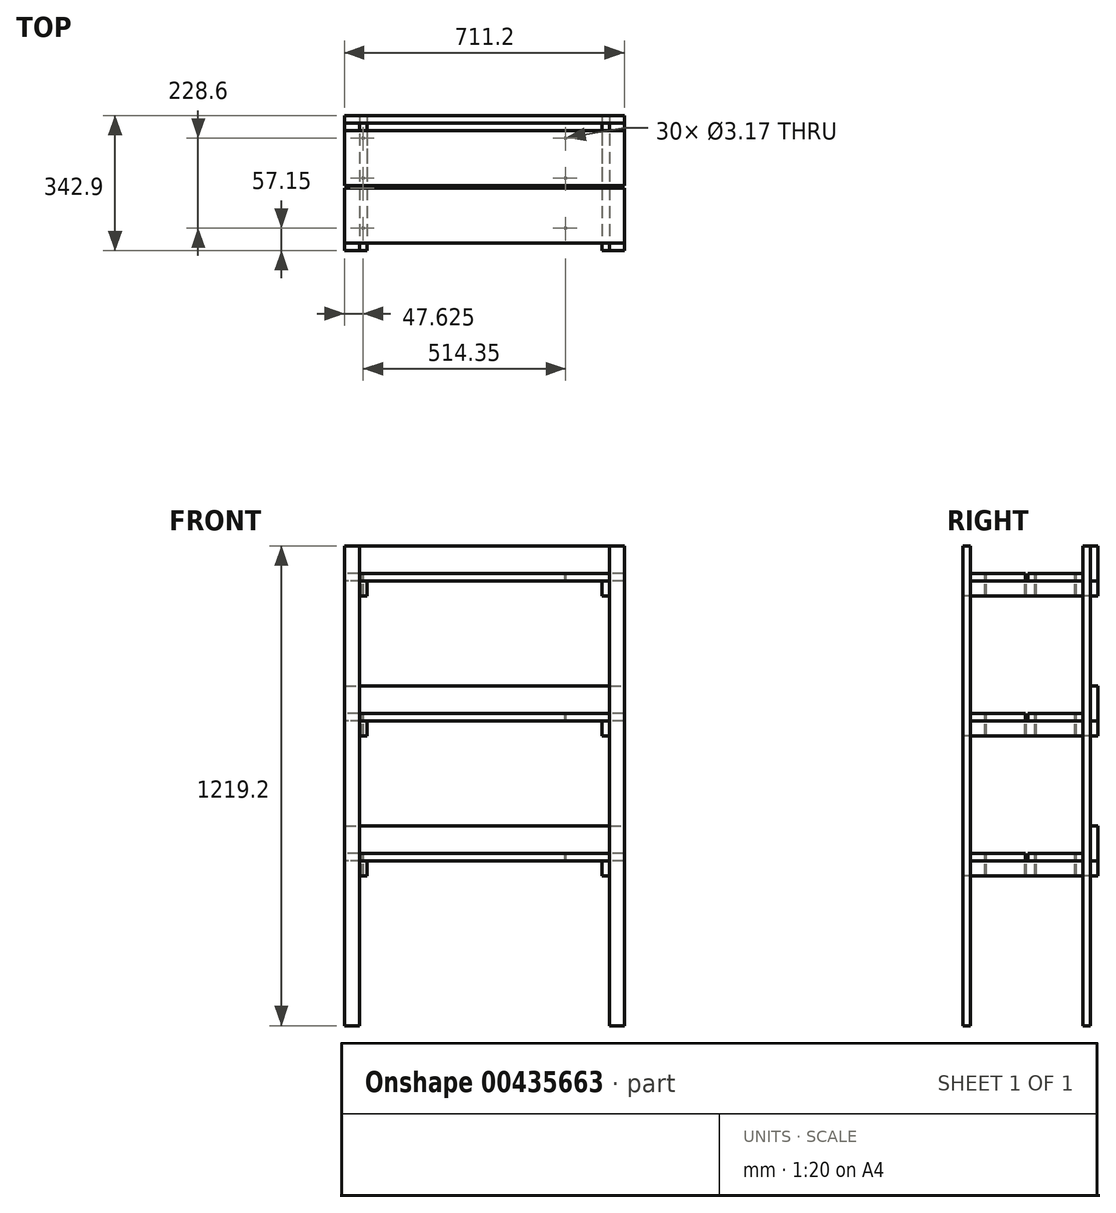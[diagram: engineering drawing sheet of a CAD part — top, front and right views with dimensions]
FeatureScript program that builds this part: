
annotation { "Feature Type Name" : "Feature", "Feature Type Description" : "" }
export const myFeature = defineFeature(function(context is Context, id is Id, definition is map)
    precondition{}
    {
        {
            var Q0;
            Q0=qCreatedBy(makeId("Top.planeOp"),FACE);
            var sketch = newSketch(context, id + "F0", { "sketchPlane" : qUnion([Q0])});
            skLineSegment(sketch, "E0.bottom", {"start": v(0, 0) * mm, "end": v(38.1, 0) * mm});
            skLineSegment(sketch, "E0.top", {"start": v(0, 19.05) * mm, "end": v(38.1, 19.05) * mm});
            skLineSegment(sketch, "E0.left", {"start": v(0, 0) * mm, "end": v(0, 19.05) * mm});
            skLineSegment(sketch, "E0.right", {"start": v(38.1, 0) * mm, "end": v(38.1, 19.05) * mm});
            skLineSegment(sketch, "E1", {"start": v(355.6, 323.85) * mm, "end": v(355.6, 0) * mm, "construction": true});
            skLineSegment(sketch, "E2", {"start": v(0, 161.93) * mm, "end": v(711.2, 161.93) * mm, "construction": true});
            skPoint(sketch, "E3", {"position": v(355.6, 161.93) * mm});
            skLineSegment(sketch, "E4.MirrorCS", {"start": v(711.2, 0) * mm, "end": v(673.1, 0) * mm});
            skLineSegment(sketch, "E5.MirrorCS", {"start": v(711.2, 0) * mm, "end": v(711.2, 19.05) * mm});
            skLineSegment(sketch, "E6.MirrorCS", {"start": v(711.2, 19.05) * mm, "end": v(673.1, 19.05) * mm});
            skLineSegment(sketch, "E7.MirrorCS", {"start": v(673.1, 0) * mm, "end": v(673.1, 19.05) * mm});
            skLineSegment(sketch, "E8.MirrorCS", {"start": v(673.1, 323.85) * mm, "end": v(673.1, 304.8) * mm});
            skLineSegment(sketch, "E9.MirrorCS", {"start": v(711.2, 323.85) * mm, "end": v(711.2, 304.8) * mm});
            skLineSegment(sketch, "E10.MirrorCS", {"start": v(0, 323.85) * mm, "end": v(0, 304.8) * mm});
            skLineSegment(sketch, "E11.MirrorCS", {"start": v(38.1, 323.85) * mm, "end": v(38.1, 304.8) * mm});
            skLineSegment(sketch, "E12.MirrorCS", {"start": v(711.2, 304.8) * mm, "end": v(673.1, 304.8) * mm});
            skLineSegment(sketch, "E13.MirrorCS", {"start": v(711.2, 323.85) * mm, "end": v(673.1, 323.85) * mm});
            skLineSegment(sketch, "E14.MirrorCS", {"start": v(0, 304.8) * mm, "end": v(38.1, 304.8) * mm});
            skLineSegment(sketch, "E15.MirrorCS", {"start": v(0, 323.85) * mm, "end": v(38.1, 323.85) * mm});
            skLineSegment(sketch, "E16", {"start": v(38.1, 304.8) * mm, "end": v(38.1, 165.1) * mm, "construction": true});
            skLineSegment(sketch, "E17", {"start": v(38.1, 165.1) * mm, "end": v(38.1, 158.75) * mm, "construction": true});
            skLineSegment(sketch, "E18", {"start": v(38.1, 158.75) * mm, "end": v(38.1, 19.05) * mm, "construction": true});
            skPoint(sketch, "E19", {"position": v(38.1, 161.93) * mm});
            skSolve(sketch);
        }
        {
            var Q0;
            Q0 = qSketchRegion(id + "F0", true);
            extrude(context, id + "F1", {"entities" : qUnion([Q0]), "depth" : 1219.2 * mm});
        }
        {
            var Q0;
            Q0=makeQuery(id+"F1.opExtrude","SWEPT_FACE",FACE,{"disambiguationData":[OSD([sQuery(id+"F0.wireOp",EDGE,"E0.bottom")])]});
            var sketch = newSketch(context, id + "F2", { "sketchPlane" : qUnion([Q0])});
            skLineSegment(sketch, "E20", {"start": v(38.1, 419.1) * mm, "end": v(673.1, 419.1) * mm, "construction": true});
            skLineSegment(sketch, "E21.bottom", {"start": v(38.1, 419.1) * mm, "end": v(57.15, 419.1) * mm});
            skLineSegment(sketch, "E21.top", {"start": v(38.1, 381) * mm, "end": v(57.15, 381) * mm});
            skLineSegment(sketch, "E21.left", {"start": v(38.1, 419.1) * mm, "end": v(38.1, 381) * mm});
            skLineSegment(sketch, "E21.right", {"start": v(57.15, 419.1) * mm, "end": v(57.15, 381) * mm});
            skLineSegment(sketch, "E22.bottom", {"start": v(673.1, 419.1) * mm, "end": v(654.05, 419.1) * mm});
            skLineSegment(sketch, "E22.top", {"start": v(673.1, 381) * mm, "end": v(654.05, 381) * mm});
            skLineSegment(sketch, "E22.left", {"start": v(673.1, 419.1) * mm, "end": v(673.1, 381) * mm});
            skLineSegment(sketch, "E22.right", {"start": v(654.05, 419.1) * mm, "end": v(654.05, 381) * mm});
            skLineSegment(sketch, "E23.0.1.0", {"start": v(38.1, 774.7) * mm, "end": v(673.1, 774.7) * mm, "construction": true});
            skLineSegment(sketch, "E23.0.1.1", {"start": v(654.05, 774.7) * mm, "end": v(654.05, 736.6) * mm});
            skLineSegment(sketch, "E23.0.1.2", {"start": v(673.1, 774.7) * mm, "end": v(673.1, 736.6) * mm});
            skLineSegment(sketch, "E23.0.1.3", {"start": v(57.15, 774.7) * mm, "end": v(57.15, 736.6) * mm});
            skLineSegment(sketch, "E23.0.1.4", {"start": v(673.1, 736.6) * mm, "end": v(654.05, 736.6) * mm});
            skLineSegment(sketch, "E23.0.1.5", {"start": v(673.1, 774.7) * mm, "end": v(654.05, 774.7) * mm});
            skLineSegment(sketch, "E23.0.1.6", {"start": v(38.1, 774.7) * mm, "end": v(38.1, 736.6) * mm});
            skLineSegment(sketch, "E23.0.1.7", {"start": v(38.1, 736.6) * mm, "end": v(57.15, 736.6) * mm});
            skLineSegment(sketch, "E23.0.1.8", {"start": v(38.1, 774.7) * mm, "end": v(57.15, 774.7) * mm});
            skLineSegment(sketch, "E23.0.2.0", {"start": v(38.1, 1130.3) * mm, "end": v(673.1, 1130.3) * mm, "construction": true});
            skLineSegment(sketch, "E23.0.2.1", {"start": v(654.05, 1130.3) * mm, "end": v(654.05, 1092.2) * mm});
            skLineSegment(sketch, "E23.0.2.2", {"start": v(673.1, 1130.3) * mm, "end": v(673.1, 1092.2) * mm});
            skLineSegment(sketch, "E23.0.2.3", {"start": v(57.15, 1130.3) * mm, "end": v(57.15, 1092.2) * mm});
            skLineSegment(sketch, "E23.0.2.4", {"start": v(673.1, 1092.2) * mm, "end": v(654.05, 1092.2) * mm});
            skLineSegment(sketch, "E23.0.2.5", {"start": v(673.1, 1130.3) * mm, "end": v(654.05, 1130.3) * mm});
            skLineSegment(sketch, "E23.0.2.6", {"start": v(38.1, 1130.3) * mm, "end": v(38.1, 1092.2) * mm});
            skLineSegment(sketch, "E23.0.2.7", {"start": v(38.1, 1092.2) * mm, "end": v(57.15, 1092.2) * mm});
            skLineSegment(sketch, "E23.0.2.8", {"start": v(38.1, 1130.3) * mm, "end": v(57.15, 1130.3) * mm});
            skLineSegment(sketch, "E23.direction1", {"start": v(38.1, 381) * mm, "end": v(63.5, 381) * mm, "construction": true});
            skLineSegment(sketch, "E23.direction2", {"start": v(38.1, 381) * mm, "end": v(38.1, 736.6) * mm, "construction": true});
            skSolve(sketch);
        }
        {
            var Q0;
            Q0=makeQuery(id+"F1.opExtrude","SWEPT_FACE",FACE,{"disambiguationData":[OSD([sQuery(id+"F0.wireOp",EDGE,"E13.MirrorCS")])]});
            cPlane(context, id + "F3", {"entities" : qUnion([Q0]), "cplaneType" : CPlaneType.OFFSET, "offset" : 19.05 * mm, "width" : 152.4 * mm, "height" : 152.4 * mm});
        }
        {
            var Q0;
            Q0 = qSketchRegion(id + "F2", true);
            var Q1;
            Q1=qCreatedBy(id+"F3.planeOp",FACE);
            extrude(context, id + "F4", {"entities" : qUnion([Q0]), "endBound" : BoundingType.UP_TO_SURFACE, "oppositeDirection" : true, "endBoundEntityFace" : qUnion([Q1]), "depth" : 25.4 * mm});
        }
        {
            var Q0;
            Q0=makeQuery(id+"F1.opExtrude","SWEPT_FACE",FACE,{"disambiguationData":[OSD([sQuery(id+"F0.wireOp",EDGE,"E0.left")])]});
            var sketch = newSketch(context, id + "F5", { "sketchPlane" : qUnion([Q0])});
            skLineSegment(sketch, "E24.bottom", {"start": v(-304.8, 419.1) * mm, "end": v(-165.1, 419.1) * mm});
            skLineSegment(sketch, "E24.top", {"start": v(-304.8, 438.15) * mm, "end": v(-165.1, 438.15) * mm});
            skLineSegment(sketch, "E24.left", {"start": v(-304.8, 419.1) * mm, "end": v(-304.8, 438.15) * mm});
            skLineSegment(sketch, "E24.right", {"start": v(-165.1, 419.1) * mm, "end": v(-165.1, 438.15) * mm});
            skLineSegment(sketch, "E25.MirrorCS", {"start": v(-19.05, 438.15) * mm, "end": v(-158.75, 438.15) * mm});
            skLineSegment(sketch, "E26.MirrorCS", {"start": v(-158.75, 419.1) * mm, "end": v(-158.75, 438.15) * mm});
            skLineSegment(sketch, "E27.MirrorCS", {"start": v(-19.05, 419.1) * mm, "end": v(-19.05, 438.15) * mm});
            skLineSegment(sketch, "E28.MirrorCS", {"start": v(-19.05, 419.1) * mm, "end": v(-158.75, 419.1) * mm});
            skLineSegment(sketch, "E29.0.1.0", {"start": v(-165.1, 774.7) * mm, "end": v(-165.1, 793.75) * mm});
            skLineSegment(sketch, "E29.0.1.1", {"start": v(-19.05, 793.75) * mm, "end": v(-158.75, 793.75) * mm});
            skLineSegment(sketch, "E29.0.1.2", {"start": v(-304.8, 793.75) * mm, "end": v(-165.1, 793.75) * mm});
            skLineSegment(sketch, "E29.0.1.3", {"start": v(-158.75, 774.7) * mm, "end": v(-158.75, 793.75) * mm});
            skLineSegment(sketch, "E29.0.1.4", {"start": v(-304.8, 774.7) * mm, "end": v(-165.1, 774.7) * mm});
            skLineSegment(sketch, "E29.0.1.5", {"start": v(-304.8, 774.7) * mm, "end": v(-304.8, 793.75) * mm});
            skLineSegment(sketch, "E29.0.1.6", {"start": v(-19.05, 774.7) * mm, "end": v(-158.75, 774.7) * mm});
            skLineSegment(sketch, "E29.0.1.7", {"start": v(-19.05, 774.7) * mm, "end": v(-19.05, 793.75) * mm});
            skLineSegment(sketch, "E29.0.2.0", {"start": v(-165.1, 1130.3) * mm, "end": v(-165.1, 1149.35) * mm});
            skLineSegment(sketch, "E29.0.2.1", {"start": v(-19.05, 1149.35) * mm, "end": v(-158.75, 1149.35) * mm});
            skLineSegment(sketch, "E29.0.2.2", {"start": v(-304.8, 1149.35) * mm, "end": v(-165.1, 1149.35) * mm});
            skLineSegment(sketch, "E29.0.2.3", {"start": v(-158.75, 1130.3) * mm, "end": v(-158.75, 1149.35) * mm});
            skLineSegment(sketch, "E29.0.2.4", {"start": v(-304.8, 1130.3) * mm, "end": v(-165.1, 1130.3) * mm});
            skLineSegment(sketch, "E29.0.2.5", {"start": v(-304.8, 1130.3) * mm, "end": v(-304.8, 1149.35) * mm});
            skLineSegment(sketch, "E29.0.2.6", {"start": v(-19.05, 1130.3) * mm, "end": v(-158.75, 1130.3) * mm});
            skLineSegment(sketch, "E29.0.2.7", {"start": v(-19.05, 1130.3) * mm, "end": v(-19.05, 1149.35) * mm});
            skLineSegment(sketch, "E29.direction1", {"start": v(-304.8, 419.1) * mm, "end": v(-279.4, 419.1) * mm, "construction": true});
            skLineSegment(sketch, "E29.direction2", {"start": v(-304.8, 419.1) * mm, "end": v(-304.8, 774.7) * mm, "construction": true});
            skSolve(sketch);
        }
        {
            var Q0;
            Q0 = qSketchRegion(id + "F5", true);
            var Q1;
            Q1=makeQuery(id+"F1.opExtrude","SWEPT_FACE",FACE,{"disambiguationData":[OSD([sQuery(id+"F0.wireOp",EDGE,"E9.MirrorCS")])]});
            extrude(context, id + "F6", {"entities" : qUnion([Q0]), "endBound" : BoundingType.UP_TO_SURFACE, "oppositeDirection" : true, "endBoundEntityFace" : qUnion([Q1]), "depth" : 25.4 * mm});
        }
        {
            var Q0;
            Q0=makeQuery(id+"F6.opExtrude","SWEPT_FACE",FACE,{"disambiguationData":[OSD([sQuery(id+"F5.wireOp",EDGE,"E29.0.2.1")])]});
            var sketch = newSketch(context, id + "F7", { "sketchPlane" : qUnion([Q0])});
            skCircle(sketch, "E30", {"center": v(47.62, 285.75) * mm, "radius": 1.59 * mm});
            skLineSegment(sketch, "E31", {"start": v(38.1, 304.8) * mm, "end": v(57.15, 165.1) * mm, "construction": true});
            skLineSegment(sketch, "E32", {"start": v(47.62, 285.75) * mm, "end": v(47.62, 184.15) * mm, "construction": true});
            skPoint(sketch, "E33", {"position": v(47.62, 234.95) * mm});
            skLineSegment(sketch, "E34", {"start": v(47.62, 234.95) * mm, "end": v(0, 234.95) * mm, "construction": true});
            skCircle(sketch, "E35.MirrorC", {"center": v(47.62, 184.15) * mm, "radius": 1.59 * mm});
            skLineSegment(sketch, "E36", {"start": v(38.1, 171.45) * mm, "end": v(57.15, 171.45) * mm, "construction": true});
            skLineSegment(sketch, "E37", {"start": v(304.8, 304.8) * mm, "end": v(304.8, 165.1) * mm, "construction": true});
            skCircle(sketch, "E38.MirrorC", {"center": v(47.62, 57.15) * mm, "radius": 1.59 * mm});
            skCircle(sketch, "E39.MirrorC", {"center": v(47.62, 158.75) * mm, "radius": 1.59 * mm});
            skCircle(sketch, "E40.MirrorC", {"center": v(561.98, 285.75) * mm, "radius": 1.59 * mm});
            skCircle(sketch, "E41.MirrorC", {"center": v(561.98, 184.15) * mm, "radius": 1.59 * mm});
            skCircle(sketch, "E42.MirrorC", {"center": v(561.98, 158.75) * mm, "radius": 1.59 * mm});
            skCircle(sketch, "E43.MirrorC", {"center": v(561.98, 57.15) * mm, "radius": 1.59 * mm});
            skSolve(sketch);
        }
        {
            var Q0;
            Q0 = qSketchRegion(id + "F7", true);
            extrude(context, id + "F8", {"entities" : qUnion([Q0]), "operationType" : NewBodyOperationType.REMOVE, "endBound" : BoundingType.THROUGH_ALL, "oppositeDirection" : true, "depth" : 25.4 * mm});
        }
        {
            var Q0;
            Q0=makeQuery(id+"F1.opExtrude","SWEPT_FACE",FACE,{"disambiguationData":[OSD([sQuery(id+"F0.wireOp",EDGE,"E9.MirrorCS")])]});
            var sketch = newSketch(context, id + "F9", { "sketchPlane" : qUnion([Q0])});
            skLineSegment(sketch, "E44.bottom", {"start": v(342.9, 419.1) * mm, "end": v(323.85, 419.1) * mm});
            skLineSegment(sketch, "E44.top", {"start": v(342.9, 508) * mm, "end": v(323.85, 508) * mm});
            skLineSegment(sketch, "E44.left", {"start": v(342.9, 419.1) * mm, "end": v(342.9, 508) * mm});
            skLineSegment(sketch, "E44.right", {"start": v(323.85, 419.1) * mm, "end": v(323.85, 508) * mm});
            skLineSegment(sketch, "E45.0.1.0", {"start": v(342.9, 774.7) * mm, "end": v(323.85, 774.7) * mm});
            skLineSegment(sketch, "E45.0.1.1", {"start": v(342.9, 774.7) * mm, "end": v(342.9, 863.6) * mm});
            skLineSegment(sketch, "E45.0.1.2", {"start": v(323.85, 774.7) * mm, "end": v(323.85, 863.6) * mm});
            skLineSegment(sketch, "E45.0.1.3", {"start": v(342.9, 863.6) * mm, "end": v(323.85, 863.6) * mm});
            skLineSegment(sketch, "E45.0.2.0", {"start": v(342.9, 1130.3) * mm, "end": v(323.85, 1130.3) * mm});
            skLineSegment(sketch, "E45.0.2.1", {"start": v(342.9, 1130.3) * mm, "end": v(342.9, 1219.2) * mm});
            skLineSegment(sketch, "E45.0.2.2", {"start": v(323.85, 1130.3) * mm, "end": v(323.85, 1219.2) * mm});
            skLineSegment(sketch, "E45.0.2.3", {"start": v(342.9, 1219.2) * mm, "end": v(323.85, 1219.2) * mm});
            skLineSegment(sketch, "E45.direction1", {"start": v(323.85, 419.1) * mm, "end": v(349.25, 419.1) * mm, "construction": true});
            skLineSegment(sketch, "E45.direction2", {"start": v(323.85, 419.1) * mm, "end": v(323.85, 774.7) * mm, "construction": true});
            skSolve(sketch);
        }
        {
            var Q0;
            Q0 = qSketchRegion(id + "F9", true);
            var Q1;
            Q1=makeQuery(id+"F1.opExtrude","SWEPT_FACE",FACE,{"disambiguationData":[OSD([sQuery(id+"F0.wireOp",EDGE,"E10.MirrorCS")])]});
            extrude(context, id + "F10", {"entities" : qUnion([Q0]), "endBound" : BoundingType.UP_TO_SURFACE, "oppositeDirection" : true, "endBoundEntityFace" : qUnion([Q1]), "depth" : 25.4 * mm});
        }
    });
